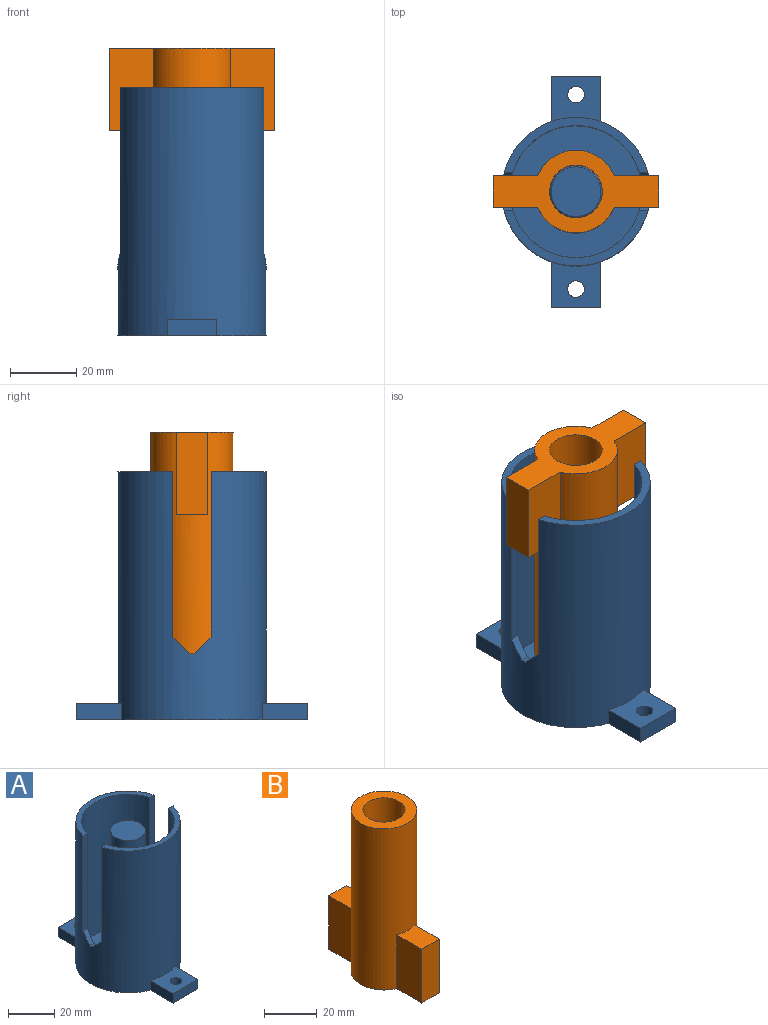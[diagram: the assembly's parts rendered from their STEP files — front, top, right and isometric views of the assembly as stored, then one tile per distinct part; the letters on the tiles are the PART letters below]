
ASSEMBLY  parts=2 mates=1
PART A: 29 faces, bbox 45x70x75 mm
  f0: cylinder r=22.5mm len=75mm, axis (0,0,-1), area 9221.7mm2, adj f1,f3,f4,f5,f6,f7,f10,f11
  f1: plane 43.51x16.75mm, normal (0,0,1), area 137.8mm2, adj f0,f2,f18,f19
  f2: cylinder r=20mm len=70mm, axis (0,0,1), area 7564.5mm2, adj f1,f12,f13,f16,f17,f18,f19,f20
  f3: plane 13.79x5mm, normal (-1,0,0), area 68.9mm2, adj f0,f7,f9,f11
  f4: plane 13.79x5mm, normal (-1,0,0), area 68.9mm2, adj f0,f8,f10,f11
  f5: plane 13.79x5mm, normal (1,0,0), area 68.9mm2, adj f0,f7,f9,f11
  f6: plane 13.79x5mm, normal (1,0,0), area 68.9mm2, adj f0,f8,f10,f11
  f7: plane 15x13.79mm, normal (0,0,1), area 174.2mm2, adj f0,f3,f5,f9,f15
  f8: plane 15x5mm, normal (0,1,0), area 75mm2, adj f4,f6,f10,f11
  f9: plane 15x5mm, normal (0,-1,0), area 75mm2, adj f3,f5,f7,f11
  f10: plane 15x13.79mm, normal (0,0,1), area 174.2mm2, adj f0,f4,f6,f8,f14
  f11: plane 70x45mm, normal (0,0,-1), area 1938.9mm2, adj f0,f3,f4,f5,f6,f8,f9,f14
  f12: plane 43.51x16.75mm, normal (0,0,1), area 137.8mm2, adj f0,f2,f17,f20
  f13: plane 40x40mm, normal (0,0,1), area 765.8mm2, adj f2,f24
  f14: cylinder r=2.5mm len=5mm, axis (0,0,1), area 78.5mm2, adj f10,f11
  f15: cylinder r=2.5mm len=5mm, axis (0,0,1), area 78.5mm2, adj f7,f11
  f16: plane 2.51x1.5mm, normal (0,0,1), area 3.8mm2, adj f0,f2,f25,f26
  f17: plane 50x2.6mm, normal (0,1,0), area 129.9mm2, adj f0,f2,f12,f26
  f18: plane 50x2.6mm, normal (0,-1,0), area 129.9mm2, adj f0,f1,f2,f25
  f19: plane 50x2.6mm, normal (0,-1,0), area 129.9mm2, adj f0,f1,f2,f28
  f20: plane 50x2.6mm, normal (0,1,0), area 129.9mm2, adj f0,f2,f12,f27
  f21: plane 2.51x1.5mm, normal (0,0,1), area 3.8mm2, adj f0,f2,f27,f28
  f22: cylinder r=7.5mm len=60mm, axis (0,0,-1), area 2827.4mm2, adj f23,f24
  f23: plane 15x15mm, normal (0,0,1), area 176.7mm2, adj f22
  f24: cone r=7.5mm half-angle=45deg, axis (0,0,-1), area 444.3mm2, adj f13,f22
  f25: plane 5x5mm, normal (0,-0.71,0.71), area 17.9mm2, adj f0,f2,f16,f18
  f26: plane 5x5mm, normal (0,0.71,0.71), area 17.9mm2, adj f0,f2,f16,f17
  f27: plane 5x5mm, normal (0,0.71,0.71), area 17.9mm2, adj f0,f2,f20,f21
  f28: plane 5x5mm, normal (0,-0.71,0.71), area 17.9mm2, adj f0,f2,f19,f21
PART B: 12 faces, bbox 25x50x75 mm
  f0: plane 25x13.44mm, normal (-1,0,0), area 335.9mm2, adj f4,f6,f8,f9
  f1: plane 25x13.44mm, normal (-1,0,0), area 335.9mm2, adj f5,f7,f8,f9
  f2: plane 25x13.44mm, normal (1,0,0), area 335.9mm2, adj f4,f6,f8,f9
  f3: plane 25x13.44mm, normal (1,0,0), area 335.9mm2, adj f5,f7,f8,f9
  f4: plane 13.44x9.5mm, normal (0,0,1), area 121.7mm2, adj f0,f2,f6,f9
  f5: plane 25x9.5mm, normal (0,1,0), area 237.5mm2, adj f1,f3,f7,f8
  f6: plane 25x9.5mm, normal (0,-1,0), area 237.5mm2, adj f0,f2,f4,f8
  f7: plane 13.44x9.5mm, normal (0,0,1), area 121.7mm2, adj f1,f3,f5,f9
  f8: plane 50x25mm, normal (0,0,-1), area 533.2mm2, adj f0,f1,f2,f3,f5,f6,f9,f11
  f9: cylinder r=12.5mm len=75mm, axis (0,0,-1), area 5403.2mm2, adj f0,f1,f2,f3,f4,f7,f8,f10
  f10: plane 25x25mm, normal (0,0,1), area 289.8mm2, adj f9,f11
  f11: cylinder r=8mm len=75mm, axis (0,0,1), area 3769.9mm2, adj f8,f10
PLACE A rot(axis=(-0.01,0,-1),0deg) t=(-13.39,-46,74.98)mm
PLACE B rot(axis=(-0.71,-0.71,0),180deg) t=(-13.39,-46,161.9)mm
MATE slider A.f22 <-> B.f9  axis (0,0,1) through (-13.39,-46,144.98)mm
